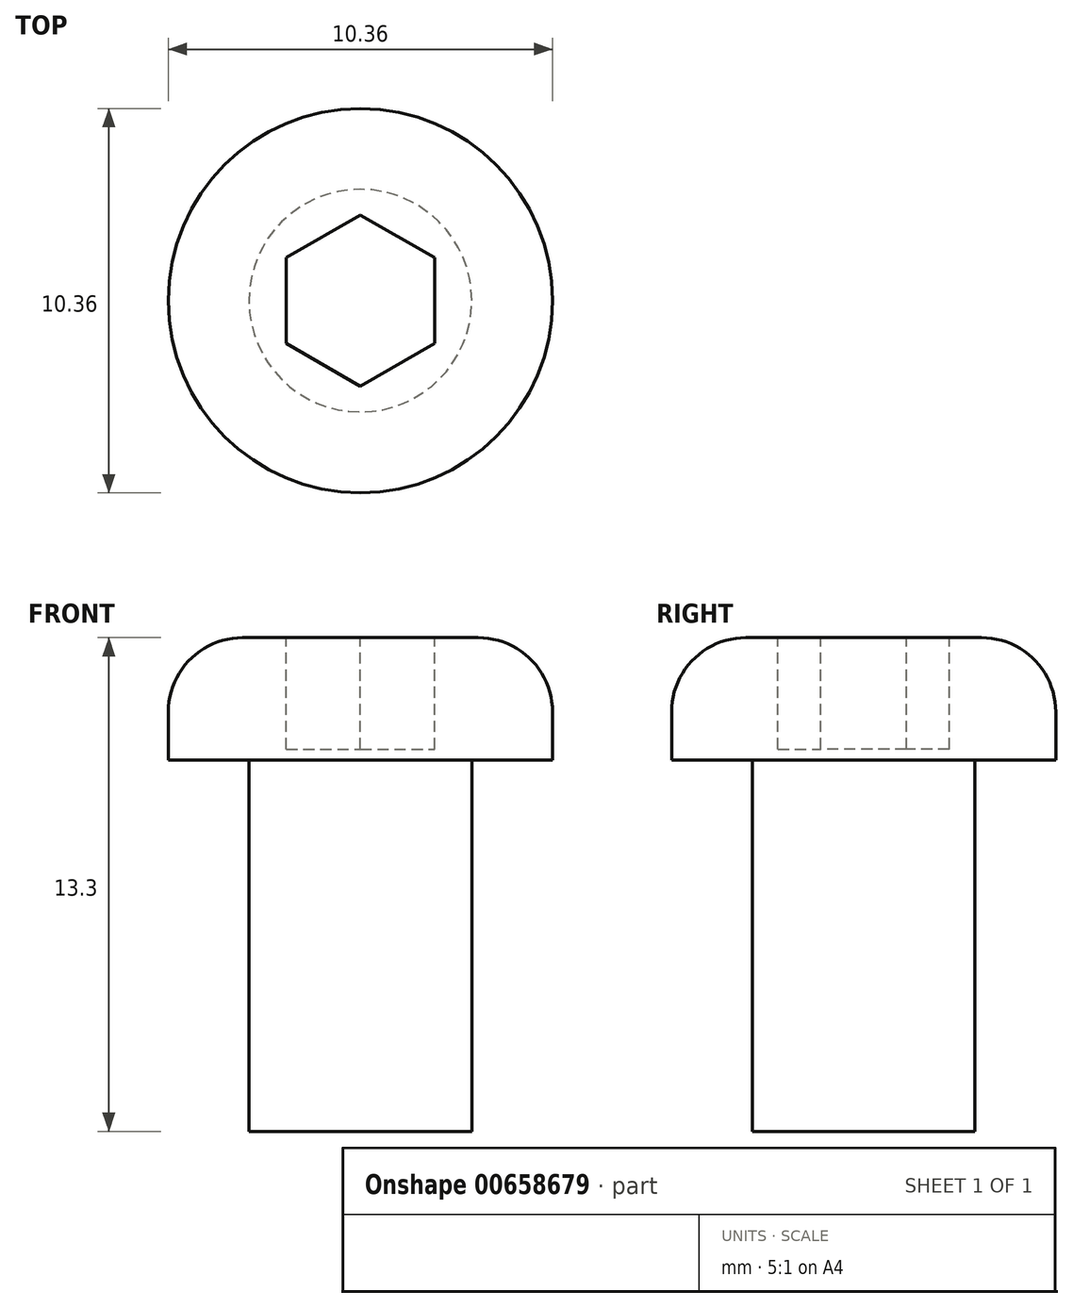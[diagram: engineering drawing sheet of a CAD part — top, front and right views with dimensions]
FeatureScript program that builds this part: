
annotation { "Feature Type Name" : "Feature", "Feature Type Description" : "" }
export const myFeature = defineFeature(function(context is Context, id is Id, definition is map)
    precondition{}
    {
        {
            var Q0;
            Q0=qCreatedBy(makeId("Top.planeOp"),FACE);
            var sketch = newSketch(context, id + "F0", { "sketchPlane" : qUnion([Q0])});
            skCircle(sketch, "E0", {"center": v(0, 0) * mm, "radius": 3 * mm});
            skSolve(sketch);
        }
        {
            var Q0;
            Q0=makeQuery(id+"F0.imprint","IMPRINT",FACE,{"disambiguationData":[TD([[makeQuery(id+"F0.imprint","IMPRINT",EDGE,{"derivedFrom":sQuery(id+"F0.wireOp",EDGE,"E0")}),1.0]])]});
            extrude(context, id + "F1", {"entities" : qUnion([Q0]), "depth" : 10 * mm});
        }
        {
            var Q0;
            Q0=makeQuery(id+"F1.opExtrude","CAP_FACE",FACE,{"disambiguationData":[OSD([sQuery(id+"F0.wireOp",EDGE,"E0")])],"isStart":false});
            var sketch = newSketch(context, id + "F2", { "sketchPlane" : qUnion([Q0])});
            skCircle(sketch, "E1", {"center": v(0, 0) * mm, "radius": 5.17 * mm});
            skSolve(sketch);
        }
        {
            var Q0;
            Q0=makeQuery(id+"F2.imprint","IMPRINT",FACE,{"disambiguationData":[TD([[makeQuery(id+"F2.imprint","IMPRINT",EDGE,{"derivedFrom":makeQuery(id+"F1.opExtrude","CAP_EDGE",EDGE,{"disambiguationData":[OSD([sQuery(id+"F0.wireOp",EDGE,"E0")])],"isStart":false})}),1.0]])]});
            var Q1;
            Q1=makeQuery(id+"F2.imprint","IMPRINT",FACE,{"disambiguationData":[TD([[makeQuery(id+"F2.imprint","IMPRINT",EDGE,{"derivedFrom":sQuery(id+"F2.wireOp",EDGE,"E1")}),1.0]])]});
            extrude(context, id + "F3", {"entities" : qUnion([Q0, Q1]), "operationType" : NewBodyOperationType.ADD, "depth" : 3.3 * mm});
        }
        {
            var Q0;
            Q0=makeQuery(id+"F3.opExtrude","CAP_EDGE",EDGE,{"disambiguationData":[OSD([sQuery(id+"F2.wireOp",EDGE,"E1")])],"isStart":false});
            fillet(context, id + "F4", {"entities" : qUnion([Q0]), "radius" : 2 * mm, "tangentPropagation" : true, "allowEdgeOverflow" : false});
        }
        {
            var Q0;
            Q0=makeQuery(id+"F3.opExtrude","CAP_FACE",FACE,{"disambiguationData":[OSD([sQuery(id+"F2.wireOp",EDGE,"E1")])],"isStart":false});
            var sketch = newSketch(context, id + "F5", { "sketchPlane" : qUnion([Q0])});
            skCircle(sketch, "E2.cCircle", {"center": v(0, 0) * mm, "radius": 2 * mm, "construction": true});
            skLineSegment(sketch, "E2.0", {"start": v(2, 1.15) * mm, "end": v(2, -1.15) * mm});
            skLineSegment(sketch, "E2.1", {"start": v(2, -1.15) * mm, "end": v(0, -2.3) * mm});
            skLineSegment(sketch, "E2.2", {"start": v(0, -2.3) * mm, "end": v(-2, -1.15) * mm});
            skLineSegment(sketch, "E2.3", {"start": v(-2, -1.15) * mm, "end": v(-2, 1.15) * mm});
            skLineSegment(sketch, "E2.4", {"start": v(-2, 1.15) * mm, "end": v(0, 2.3) * mm});
            skLineSegment(sketch, "E2.5", {"start": v(0, 2.3) * mm, "end": v(2, 1.15) * mm});
            skPoint(sketch, "E2.0.midPoint", {"position": v(2, 0) * mm});
            skSolve(sketch);
        }
        {
            var Q0;
            Q0=makeQuery(id+"F5.imprint","IMPRINT",FACE,{"disambiguationData":[TD([[makeQuery(id+"F5.imprint","IMPRINT",EDGE,{"derivedFrom":sQuery(id+"F5.wireOp",EDGE,"E2.0")}),-1.0]])]});
            extrude(context, id + "F6", {"entities" : qUnion([Q0]), "operationType" : NewBodyOperationType.REMOVE, "oppositeDirection" : true, "depth" : 3 * mm});
        }
    });
